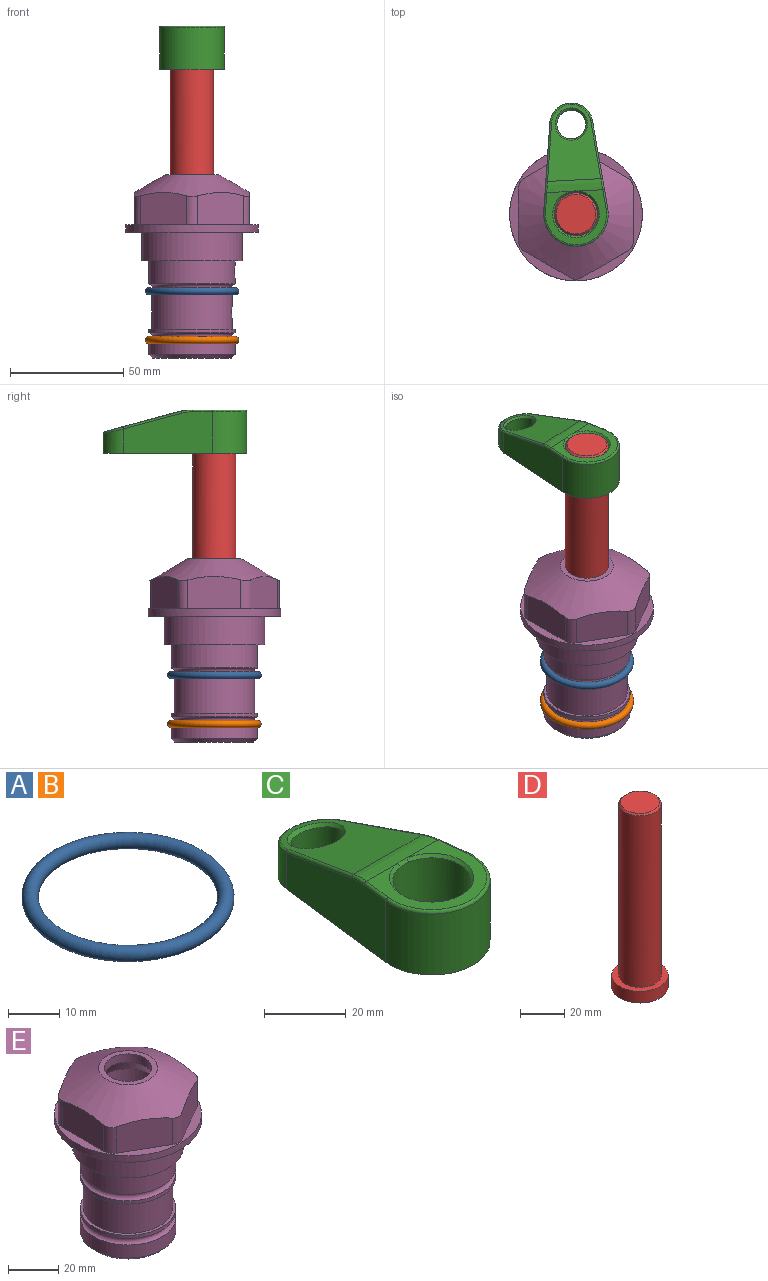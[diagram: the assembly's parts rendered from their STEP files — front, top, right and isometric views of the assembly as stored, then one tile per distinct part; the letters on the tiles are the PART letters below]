
ASSEMBLY  parts=5 mates=4
PART A: 1 faces, bbox 44.7x44.7x3.2 mm
  f0: torus R=19.05mm, axis (0,0,1), area 1193.9mm2
PART B: same geometry as A
PART C: 31 faces, bbox 31.7x65.5x19.8 mm
  f0: plane 39.12x18.26mm, normal (0.99,0.12,0), area 612.2mm2, adj f1,f4,f7,f11,f13,f15
  f1: cylinder r=9.53mm len=18.91mm, axis (0,0,-1), area 296.1mm2, adj f0,f2,f7,f17
  f2: plane 39.12x18.26mm, normal (-0.99,0.12,0), area 612.2mm2, adj f1,f4,f7,f12,f14,f16
  f3: cylinder r=6.35mm len=12.7mm, axis (0,0,-1), area 362.4mm2, adj f7,f18
  f4: cylinder r=14.29mm len=28.58mm, axis (0,0,-1), area 882.2mm2, adj f0,f2,f7,f10
  f5: cylinder r=9.53mm len=19.05mm, axis (0,0,-1), area 1092.6mm2, adj f7,f19,f20
  f6: plane 26.99x23.69mm, normal (0,0,1), area 216.2mm2, adj f9,f10,f11,f12,f19
  f7: plane 63.5x28.58mm, normal (0,0,-1), area 661.8mm2, adj f0,f1,f2,f3,f4,f5,f22,f23
  f8: plane 33.52x23.6mm, normal (0,0.26,0.97), area 486mm2, adj f9,f15,f16,f17,f18
  f9: cylinder r=19.05mm len=24.72mm, axis (1,0,0), area 120.4mm2, adj f6,f8,f13,f14,f20
  f10: torus R=13.49mm, axis (0,0,1), area 59mm2, adj f4,f6,f11,f12
  f11: cylinder r=0.79mm len=8.67mm, axis (0.12,-0.99,0), area 10.8mm2, adj f0,f6,f10,f13
  f12: cylinder r=0.79mm len=8.67mm, axis (0.12,0.99,0), area 10.8mm2, adj f2,f6,f10,f14
  f13: bspline ~4.95x1.42mm, area 6.1mm2, adj f0,f9,f11,f15
  f14: bspline ~4.95x1.42mm, area 6.1mm2, adj f2,f9,f12,f16
  f15: cylinder r=0.79mm len=25.95mm, axis (0.12,-0.96,0.26), area 32.9mm2, adj f0,f8,f13,f17
  f16: cylinder r=0.79mm len=25.95mm, axis (0.12,0.96,-0.26), area 32.9mm2, adj f2,f8,f14,f17
  f17: bspline ~18.91x8.38mm, area 30mm2, adj f1,f8,f15,f16
  f18: bspline ~14.29x14.29mm, area 48.3mm2, adj f3,f8
  f19: cone r=9.53mm half-angle=45deg, axis (0,0,1), area 66.5mm2, adj f5,f6,f20
  f20: bspline ~3.22x0.96mm, area 3.5mm2, adj f5,f9,f19
  f21: plane 2.75x2.72mm, normal (0,0,-1), area 2.9mm2, adj f23,f25,f28
  f22: plane 23.05x15.88mm, normal (-0.99,-0.12,0), area 323.6mm2, adj f7,f25,f26,f27,f28,f29
  f23: plane 23.05x15.88mm, normal (0.99,-0.12,0), area 323.6mm2, adj f7,f21,f25,f27,f28,f30
  f24: cylinder r=9.53mm len=10.69mm, axis (0,0,-1), area 114.7mm2, adj f7,f27,f29,f30
  f25: cylinder r=12.7mm len=20.59mm, axis (0,0,-1), area 381.1mm2, adj f7,f21,f22,f23,f26,f28
  f26: plane 2.75x2.72mm, normal (0,0,-1), area 2.9mm2, adj f22,f25,f28
  f27: plane 19.72x18.37mm, normal (0,-0.26,-0.97), area 291.8mm2, adj f22,f23,f24,f28,f29,f30
  f28: cylinder r=15.88mm len=19.92mm, axis (1,0,0), area 54.8mm2, adj f21,f22,f23,f25,f26,f27
  f29: cylinder r=1.59mm len=11mm, axis (0,0,-1), area 34.7mm2, adj f7,f22,f24,f27
  f30: cylinder r=1.59mm len=11mm, axis (0,0,-1), area 34.7mm2, adj f7,f23,f24,f27
PART D: 6 faces, bbox 25.4x25.4x101.6 mm
  f0: plane 17.46x17.46mm, normal (0,0,1), area 239.5mm2, adj f5
  f1: plane 25.4x25.4mm, normal (0,0,-1), area 506.7mm2, adj f2
  f2: cylinder r=12.7mm len=25.4mm, axis (0,0,1), area 506.7mm2, adj f1,f3
  f3: plane 25.4x25.4mm, normal (0,0,1), area 221.7mm2, adj f2,f4
  f4: cylinder r=9.53mm len=94.46mm, axis (0,0,1), area 5653mm2, adj f3,f5
  f5: cone r=8.73mm half-angle=45deg, axis (0,0,-1), area 64.4mm2, adj f0,f4
PART E: 36 faces, bbox 58.7x58.7x81 mm
  f0: cylinder r=17.78mm len=35.56mm, axis (0,0,1), area 1670.8mm2, adj f23,f24,f31
  f1: cylinder r=19.05mm len=38.1mm, axis (0,0,1), area 1191.9mm2, adj f26,f27,f30
  f2: plane 58.66x58.66mm, normal (0,0,-1), area 1150.6mm2, adj f3,f28
  f3: cylinder r=29.33mm len=58.66mm, axis (0,0,-1), area 585.1mm2, adj f2,f4
  f4: plane 58.66x58.66mm, normal (0,0,1), area 475.9mm2, adj f3,f5,f6,f7,f8,f9,f10,f11
  f5: plane 20.32x14.34mm, normal (-0.5,0.87,0), area 324.4mm2, adj f4,f15,f16,f17
  f6: plane 20.32x14.34mm, normal (0.5,0.87,0), area 324.4mm2, adj f4,f14,f15,f17
  f7: plane 23.48x14.34mm, normal (1,0,0), area 324.4mm2, adj f4,f13,f14,f17
  f8: plane 20.32x14.34mm, normal (0.5,-0.87,0), area 324.4mm2, adj f4,f12,f13,f17
  f9: plane 20.32x14.34mm, normal (-0.5,-0.87,0), area 324.4mm2, adj f4,f11,f12,f17
  f10: plane 23.48x14.34mm, normal (-1,0,0), area 324.4mm2, adj f4,f11,f16,f17
  f11: cylinder r=5.08mm len=12.85mm, axis (0,0,-1), area 67.2mm2, adj f4,f9,f10,f17
  f12: cylinder r=5.08mm len=12.85mm, axis (0,0,-1), area 67.2mm2, adj f4,f8,f9,f17
  f13: cylinder r=5.08mm len=12.85mm, axis (0,0,-1), area 67.2mm2, adj f4,f7,f8,f17
  f14: cylinder r=5.08mm len=12.85mm, axis (0,0,-1), area 67.2mm2, adj f4,f6,f7,f17
  f15: cylinder r=5.08mm len=12.85mm, axis (0,0,-1), area 67.2mm2, adj f4,f5,f6,f17
  f16: cylinder r=5.08mm len=12.85mm, axis (0,0,-1), area 67.2mm2, adj f4,f5,f10,f17
  f17: cone r=11.73mm half-angle=60deg, axis (0,0,-1), area 2071.8mm2, adj f5,f6,f7,f8,f9,f10,f11,f12
  f18: plane 23.46x23.46mm, normal (0,0,1), area 147.4mm2, adj f17,f35
  f19: plane 34.93x34.93mm, normal (0,0,-1), area 958mm2, adj f29
  f20: cylinder r=19.05mm len=38.1mm, axis (0,0,1), area 760.1mm2, adj f21,f29
  f21: torus R=19.05mm, axis (0,0,1), area 565.3mm2, adj f20,f22
  f22: cylinder r=19.05mm len=38.1mm, axis (0,0,1), area 190mm2, adj f21,f23
  f23: plane 38.1x38.1mm, normal (0,0,1), area 146.9mm2, adj f0,f22
  f24: plane 38.1x38.1mm, normal (0,0,-1), area 146.9mm2, adj f0,f25
  f25: cylinder r=19.05mm len=38.1mm, axis (0,0,1), area 190mm2, adj f24,f26
  f26: torus R=19.05mm, axis (0,0,1), area 565.3mm2, adj f1,f25
  f27: plane 44.45x44.45mm, normal (0,0,-1), area 411.7mm2, adj f1,f28
  f28: cylinder r=22.23mm len=44.45mm, axis (0,0,1), area 1773.5mm2, adj f2,f27
  f29: cone r=19.05mm half-angle=45deg, axis (0,0,1), area 257.5mm2, adj f19,f20
  f30: cylinder r=3.17mm len=6.75mm, axis (-1,0,0), area 128mm2, adj f1,f33
  f31: cylinder r=3.17mm len=6.35mm, axis (-1,0,0), area 102.5mm2, adj f0,f33
  f32: plane 25.4x25.4mm, normal (0,0,1), area 506.7mm2, adj f33
  f33: cylinder r=12.7mm len=66.42mm, axis (0,0,-1), area 5236.2mm2, adj f30,f31,f32,f34
  f34: cone r=9.53mm half-angle=30deg, axis (0,0,-1), area 443.4mm2, adj f33,f35
  f35: cylinder r=9.53mm len=19.05mm, axis (0,0,-1), area 240.9mm2, adj f18,f34
PLACE A t=(0,0,-1.59)mm
PLACE B t=(0,0,-23.18)mm
PLACE C rot(axis=(0,0,1),3deg) t=(0,0,27.55)mm
PLACE D rot(axis=(0,0,1),3deg) t=(0,0,27.55)mm
PLACE E at identity fixed
MATE fastened D.f2 <-> C.f4  axis (0,0,1) through (0,0,91.05)mm
MATE fastened A.f0 <-> E.f0  axis (0,0,1) through (0,0,-26.1)mm
MATE fastened B.f0 <-> E.f0  axis (0,0,1) through (0,0,-47.69)mm
MATE cylindrical D.f2 <-> E.f0  axis (0,0,-1) through (0,0,-10.55)mm
